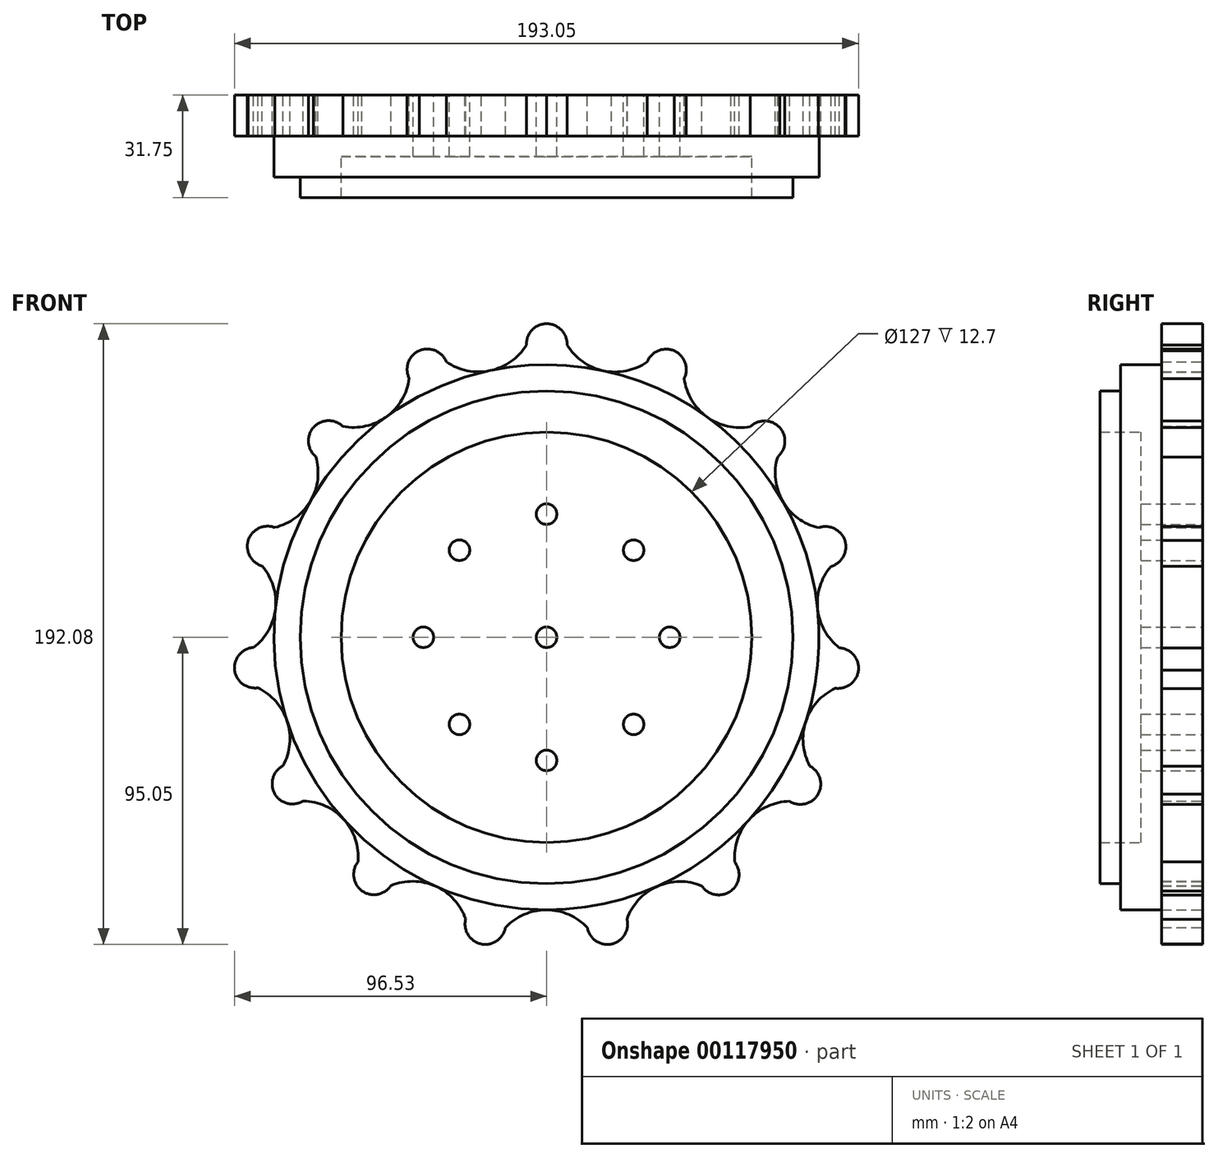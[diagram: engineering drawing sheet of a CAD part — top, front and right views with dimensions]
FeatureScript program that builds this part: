
annotation { "Feature Type Name" : "Feature", "Feature Type Description" : "" }
export const myFeature = defineFeature(function(context is Context, id is Id, definition is map)
    precondition{}
    {
        {
            var Q0;
            Q0=qCreatedBy(makeId("Front.planeOp"),FACE);
            var sketch = newSketch(context, id + "F0", { "sketchPlane" : qUnion([Q0])});
            skCircle(sketch, "E0", {"center": v(0, 0) * mm, "radius": 84.33 * mm});
            skCircle(sketch, "E1", {"center": v(0, 0) * mm, "radius": 97.03 * mm, "construction": true});
            skLineSegment(sketch, "E2", {"start": v(0, 84.33) * mm, "end": v(0, 97.03) * mm, "construction": true});
            skPoint(sketch, "E3", {"position": v(0, 90.68) * mm});
            skCircle(sketch, "E4", {"center": v(0, 0) * mm, "radius": 90.68 * mm, "construction": true});
            skArc(sketch, "E5", {"start": v(0, 90.68) * mm, "mid": v(0, 90.46) * mm, "end": v(0, 90.23) * mm});
            skPoint(sketch, "E6", {"position": v(0, 84.33) * mm});
            skPoint(sketch, "E7", {"position": v(-6.35, 90.46) * mm});
            skPoint(sketch, "E8", {"position": v(17.59, 82.47) * mm});
            skArc(sketch, "E9", {"start": v(6.35, 90.46) * mm, "mid": v(17.59, 82.47) * mm, "end": v(31.11, 85.17) * mm});
            skArc(sketch, "E10", {"start": v(6.35, 90.46) * mm, "mid": v(4.57, 95.09) * mm, "end": v(0, 97.03) * mm});
            skPoint(sketch, "E11", {"position": v(39.59, 88.59) * mm});
            skArc(sketch, "E12", {"start": v(39.59, 88.59) * mm, "mid": v(34.62, 88.68) * mm, "end": v(31.11, 85.17) * mm});
            skArc(sketch, "E13.1.0", {"start": v(-31, 85.22) * mm, "mid": v(-34.5, 88.73) * mm, "end": v(-39.46, 88.64) * mm});
            skArc(sketch, "E13.1.1", {"start": v(-31, 85.22) * mm, "mid": v(-17.48, 82.5) * mm, "end": v(-6.22, 90.46) * mm});
            skArc(sketch, "E13.1.2", {"start": v(0.13, 97.03) * mm, "mid": v(-4.44, 95.1) * mm, "end": v(-6.22, 90.46) * mm});
            skArc(sketch, "E13.2.0", {"start": v(-62.98, 65.24) * mm, "mid": v(-67.6, 67.02) * mm, "end": v(-72.1, 64.92) * mm});
            skArc(sketch, "E13.2.1", {"start": v(-62.98, 65.24) * mm, "mid": v(-49.52, 68.26) * mm, "end": v(-42.48, 80.11) * mm});
            skArc(sketch, "E13.2.2", {"start": v(-39.34, 88.7) * mm, "mid": v(-42.73, 85.07) * mm, "end": v(-42.48, 80.11) * mm});
            skArc(sketch, "E13.3.0", {"start": v(-84.07, 33.99) * mm, "mid": v(-89.02, 33.73) * mm, "end": v(-92.28, 29.98) * mm});
            skArc(sketch, "E13.3.1", {"start": v(-84.07, 33.99) * mm, "mid": v(-73, 42.21) * mm, "end": v(-71.4, 55.9) * mm});
            skArc(sketch, "E13.3.2", {"start": v(-72.02, 65.02) * mm, "mid": v(-73.64, 60.33) * mm, "end": v(-71.4, 55.9) * mm});
            skArc(sketch, "E13.4.0", {"start": v(-90.62, -3.14) * mm, "mid": v(-95.05, -5.4) * mm, "end": v(-96.5, -10.14) * mm});
            skArc(sketch, "E13.4.1", {"start": v(-90.62, -3.14) * mm, "mid": v(-83.86, 8.87) * mm, "end": v(-87.96, 22.04) * mm});
            skArc(sketch, "E13.4.2", {"start": v(-92.24, 30.11) * mm, "mid": v(-91.81, 25.17) * mm, "end": v(-87.96, 22.04) * mm});
            skArc(sketch, "E13.5.0", {"start": v(-81.5, -39.73) * mm, "mid": v(-84.63, -43.59) * mm, "end": v(-84.03, -48.51) * mm});
            skArc(sketch, "E13.5.1", {"start": v(-81.5, -39.73) * mm, "mid": v(-80.22, -26) * mm, "end": v(-89.32, -15.64) * mm});
            skArc(sketch, "E13.5.2", {"start": v(-96.51, -10) * mm, "mid": v(-94.11, -14.35) * mm, "end": v(-89.32, -15.64) * mm});
            skArc(sketch, "E13.6.0", {"start": v(-58.3, -69.45) * mm, "mid": v(-59.59, -74.24) * mm, "end": v(-57.03, -78.5) * mm});
            skArc(sketch, "E13.6.1", {"start": v(-58.3, -69.45) * mm, "mid": v(-62.7, -56.38) * mm, "end": v(-75.23, -50.62) * mm});
            skArc(sketch, "E13.6.2", {"start": v(-84.1, -48.4) * mm, "mid": v(-80.14, -51.4) * mm, "end": v(-75.23, -50.62) * mm});
            skArc(sketch, "E13.7.0", {"start": v(-25.01, -87.16) * mm, "mid": v(-24.24, -92.06) * mm, "end": v(-20.17, -94.9) * mm});
            skArc(sketch, "E13.7.1", {"start": v(-25.01, -87.16) * mm, "mid": v(-34.35, -77.01) * mm, "end": v(-48.14, -76.84) * mm});
            skArc(sketch, "E13.7.2", {"start": v(-57.14, -78.42) * mm, "mid": v(-52.3, -79.54) * mm, "end": v(-48.14, -76.84) * mm});
            skArc(sketch, "E13.8.0", {"start": v(12.6, -89.8) * mm, "mid": v(15.3, -93.96) * mm, "end": v(20.17, -94.9) * mm});
            skArc(sketch, "E13.8.1", {"start": v(12.6, -89.8) * mm, "mid": v(-0.06, -84.33) * mm, "end": v(-12.72, -89.78) * mm});
            skArc(sketch, "E13.8.2", {"start": v(-20.3, -94.88) * mm, "mid": v(-15.43, -93.94) * mm, "end": v(-12.72, -89.78) * mm});
            skArc(sketch, "E13.9.0", {"start": v(48.03, -76.91) * mm, "mid": v(52.2, -79.61) * mm, "end": v(57.03, -78.5) * mm});
            skArc(sketch, "E13.9.1", {"start": v(48.03, -76.91) * mm, "mid": v(34.25, -77.06) * mm, "end": v(24.9, -87.2) * mm});
            skArc(sketch, "E13.9.2", {"start": v(20.04, -94.94) * mm, "mid": v(24.11, -92.1) * mm, "end": v(24.9, -87.2) * mm});
            skArc(sketch, "E13.10.0", {"start": v(75.16, -50.72) * mm, "mid": v(80.07, -51.5) * mm, "end": v(84.03, -48.51) * mm});
            skArc(sketch, "E13.10.1", {"start": v(75.16, -50.72) * mm, "mid": v(62.63, -56.47) * mm, "end": v(58.2, -69.53) * mm});
            skArc(sketch, "E13.10.2", {"start": v(56.92, -78.58) * mm, "mid": v(59.49, -74.33) * mm, "end": v(58.2, -69.53) * mm});
            skArc(sketch, "E13.11.0", {"start": v(89.3, -15.77) * mm, "mid": v(94.1, -14.48) * mm, "end": v(96.5, -10.14) * mm});
            skArc(sketch, "E13.11.1", {"start": v(89.3, -15.77) * mm, "mid": v(80.18, -26.11) * mm, "end": v(81.46, -39.84) * mm});
            skArc(sketch, "E13.11.2", {"start": v(83.96, -48.63) * mm, "mid": v(84.57, -43.7) * mm, "end": v(81.46, -39.84) * mm});
            skArc(sketch, "E13.12.0", {"start": v(87.99, 21.92) * mm, "mid": v(91.85, 25.04) * mm, "end": v(92.28, 29.98) * mm});
            skArc(sketch, "E13.12.1", {"start": v(87.99, 21.92) * mm, "mid": v(83.87, 8.76) * mm, "end": v(90.62, -3.27) * mm});
            skArc(sketch, "E13.12.2", {"start": v(96.48, -10.27) * mm, "mid": v(95.04, -5.53) * mm, "end": v(90.62, -3.27) * mm});
            skArc(sketch, "E13.13.0", {"start": v(71.47, 55.81) * mm, "mid": v(73.72, 60.23) * mm, "end": v(72.1, 64.92) * mm});
            skArc(sketch, "E13.13.1", {"start": v(71.47, 55.81) * mm, "mid": v(73.06, 42.11) * mm, "end": v(84.11, 33.87) * mm});
            skArc(sketch, "E13.13.2", {"start": v(92.32, 29.86) * mm, "mid": v(89.07, 33.6) * mm, "end": v(84.11, 33.87) * mm});
            skArc(sketch, "E13.14.0", {"start": v(42.59, 80.05) * mm, "mid": v(42.85, 85) * mm, "end": v(39.46, 88.64) * mm});
            skArc(sketch, "E13.14.1", {"start": v(42.59, 80.05) * mm, "mid": v(49.61, 68.19) * mm, "end": v(63.06, 65.16) * mm});
            skArc(sketch, "E13.14.2", {"start": v(72.2, 64.83) * mm, "mid": v(67.7, 66.93) * mm, "end": v(63.06, 65.16) * mm});
            skCircle(sketch, "E14", {"center": v(0, 0) * mm, "radius": 76.2 * mm});
            skCircle(sketch, "E15", {"center": v(0, 0) * mm, "radius": 63.5 * mm});
            skCircle(sketch, "E16", {"center": v(0, 0) * mm, "radius": 38.1 * mm, "construction": true});
            skPoint(sketch, "E17", {"position": v(0, 38.1) * mm});
            skCircle(sketch, "E18", {"center": v(0, 38.1) * mm, "radius": 3.18 * mm});
            skCircle(sketch, "E19.1.0", {"center": v(-26.94, 26.94) * mm, "radius": 3.18 * mm});
            skCircle(sketch, "E19.2.0", {"center": v(-38.1, 0) * mm, "radius": 3.18 * mm});
            skCircle(sketch, "E19.3.0", {"center": v(-26.94, -26.94) * mm, "radius": 3.18 * mm});
            skCircle(sketch, "E19.4.0", {"center": v(0, -38.1) * mm, "radius": 3.18 * mm});
            skCircle(sketch, "E19.5.0", {"center": v(26.94, -26.94) * mm, "radius": 3.18 * mm});
            skCircle(sketch, "E19.6.0", {"center": v(38.1, 0) * mm, "radius": 3.18 * mm});
            skCircle(sketch, "E19.7.0", {"center": v(26.94, 26.94) * mm, "radius": 3.18 * mm});
            skCircle(sketch, "E20", {"center": v(0, 0) * mm, "radius": 3.18 * mm});
            skSolve(sketch);
        }
        {
            var Q0;
            Q0=makeQuery(id+"F0.imprint","IMPRINT",FACE,{"disambiguationData":[TD([[makeQuery(id+"F0.imprint","IMPRINT",EDGE,{"derivedFrom":sQuery(id+"F0.wireOp",EDGE,"E14")}),-1.0]])]});
            extrude(context, id + "F1", {"entities" : qUnion([Q0]), "depth" : 25.4 * mm});
        }
        {
            var Q0;
            Q0=makeQuery(id+"F0.imprint","IMPRINT",FACE,{"disambiguationData":[TD([[makeQuery(id+"F0.imprint","IMPRINT",EDGE,{"derivedFrom":sQuery(id+"F0.wireOp",EDGE,"E14")}),1.0]])]});
            extrude(context, id + "F2", {"entities" : qUnion([Q0]), "operationType" : NewBodyOperationType.ADD, "depth" : 31.75 * mm});
        }
        {
            var Q0;
            Q0=makeQuery(id+"F0.imprint","IMPRINT",FACE,{"disambiguationData":[TD([[makeQuery(id+"F0.imprint","IMPRINT",EDGE,{"derivedFrom":sQuery(id+"F0.wireOp",EDGE,"E15")}),1.0]])]});
            extrude(context, id + "F3", {"entities" : qUnion([Q0]), "operationType" : NewBodyOperationType.ADD, "depth" : 19.05 * mm});
        }
        {
            var Q0;
            {var subQ3=sQuery(id+"F0.wireOp",EDGE,"E0");var subQ5=sQuery(id+"F0.wireOp",EDGE,"E13.3.1");var subQ8=makeQuery(id+"F0.imprint","INTERSECT",VERTEX,{"derivedFrom":[subQ3,subQ5]});Q0=makeQuery(id+"F0.imprint","IMPRINT",FACE,{"disambiguationData":[TD([[makeQuery(id+"F0.imprint","IMPRINT",EDGE,{"disambiguationData":[TD([[subQ8,-1.0]])],"derivedFrom":subQ3}),-1.0]])]});}
            var Q1;
            {var subQ0=sQuery(id+"F0.wireOp",EDGE,"E13.4.1");var subQ3=sQuery(id+"F0.wireOp",EDGE,"E0");var subQ4=makeQuery(id+"F0.imprint","INTERSECT",VERTEX,{"derivedFrom":[subQ3,subQ0]});Q1=makeQuery(id+"F0.imprint","IMPRINT",FACE,{"disambiguationData":[TD([[makeQuery(id+"F0.imprint","IMPRINT",EDGE,{"disambiguationData":[TD([[subQ4,-1.0]])],"derivedFrom":subQ3}),-1.0]])]});}
            var Q2;
            {var subQ3=sQuery(id+"F0.wireOp",EDGE,"E0");var subQ5=sQuery(id+"F0.wireOp",EDGE,"E13.6.1");var subQ9=makeQuery(id+"F0.imprint","INTERSECT",VERTEX,{"derivedFrom":[subQ3,subQ5]});Q2=makeQuery(id+"F0.imprint","IMPRINT",FACE,{"disambiguationData":[TD([[makeQuery(id+"F0.imprint","IMPRINT",EDGE,{"disambiguationData":[TD([[subQ9,-1.0]])],"derivedFrom":subQ3}),-1.0]])]});}
            var Q3;
            {var subQ0=sQuery(id+"F0.wireOp",EDGE,"E13.5.1");var subQ3=sQuery(id+"F0.wireOp",EDGE,"E0");var subQ4=makeQuery(id+"F0.imprint","INTERSECT",VERTEX,{"derivedFrom":[subQ3,subQ0]});Q3=makeQuery(id+"F0.imprint","IMPRINT",FACE,{"disambiguationData":[TD([[makeQuery(id+"F0.imprint","IMPRINT",EDGE,{"disambiguationData":[TD([[subQ4,-1.0]])],"derivedFrom":subQ3}),-1.0]])]});}
            var Q4;
            {var subQ3=sQuery(id+"F0.wireOp",EDGE,"E0");var subQ5=sQuery(id+"F0.wireOp",EDGE,"E13.7.1");var subQ8=makeQuery(id+"F0.imprint","INTERSECT",VERTEX,{"derivedFrom":[subQ3,subQ5]});Q4=makeQuery(id+"F0.imprint","IMPRINT",FACE,{"disambiguationData":[TD([[makeQuery(id+"F0.imprint","IMPRINT",EDGE,{"disambiguationData":[TD([[subQ8,-1.0]])],"derivedFrom":subQ3}),-1.0]])]});}
            var Q5;
            {var subQ3=sQuery(id+"F0.wireOp",EDGE,"E0");var subQ5=sQuery(id+"F0.wireOp",EDGE,"E13.8.1");var subQ8=makeQuery(id+"F0.imprint","INTERSECT",VERTEX,{"derivedFrom":[subQ3,subQ5]});Q5=makeQuery(id+"F0.imprint","IMPRINT",FACE,{"disambiguationData":[TD([[makeQuery(id+"F0.imprint","IMPRINT",EDGE,{"disambiguationData":[TD([[subQ8,-1.0]])],"derivedFrom":subQ3}),-1.0]])]});}
            var Q6;
            {var subQ0=sQuery(id+"F0.wireOp",EDGE,"E13.9.1");var subQ3=sQuery(id+"F0.wireOp",EDGE,"E0");var subQ4=makeQuery(id+"F0.imprint","INTERSECT",VERTEX,{"derivedFrom":[subQ3,subQ0]});Q6=makeQuery(id+"F0.imprint","IMPRINT",FACE,{"disambiguationData":[TD([[makeQuery(id+"F0.imprint","IMPRINT",EDGE,{"disambiguationData":[TD([[subQ4,-1.0]])],"derivedFrom":subQ3}),-1.0]])]});}
            var Q7;
            {var subQ3=sQuery(id+"F0.wireOp",EDGE,"E0");var subQ5=sQuery(id+"F0.wireOp",EDGE,"E13.10.1");var subQ8=makeQuery(id+"F0.imprint","INTERSECT",VERTEX,{"derivedFrom":[subQ3,subQ5]});Q7=makeQuery(id+"F0.imprint","IMPRINT",FACE,{"disambiguationData":[TD([[makeQuery(id+"F0.imprint","IMPRINT",EDGE,{"disambiguationData":[TD([[subQ8,-1.0]])],"derivedFrom":subQ3}),-1.0]])]});}
            var Q8;
            {var subQ1=sQuery(id+"F0.wireOp",EDGE,"E13.12.1");var subQ3=sQuery(id+"F0.wireOp",EDGE,"E0");var subQ4=makeQuery(id+"F0.imprint","INTERSECT",VERTEX,{"derivedFrom":[subQ3,subQ1]});Q8=makeQuery(id+"F0.imprint","IMPRINT",FACE,{"disambiguationData":[TD([[makeQuery(id+"F0.imprint","IMPRINT",EDGE,{"disambiguationData":[TD([[subQ4,1.0]])],"derivedFrom":subQ3}),-1.0]])]});}
            var Q9;
            {var subQ3=sQuery(id+"F0.wireOp",EDGE,"E0");var subQ7=sQuery(id+"F0.wireOp",EDGE,"E13.13.1");var subQ9=makeQuery(id+"F0.imprint","INTERSECT",VERTEX,{"derivedFrom":[subQ3,subQ7]});Q9=makeQuery(id+"F0.imprint","IMPRINT",FACE,{"disambiguationData":[TD([[makeQuery(id+"F0.imprint","IMPRINT",EDGE,{"disambiguationData":[TD([[subQ9,1.0]])],"derivedFrom":subQ3}),-1.0]])]});}
            var Q10;
            {var subQ3=sQuery(id+"F0.wireOp",EDGE,"E0");var subQ5=sQuery(id+"F0.wireOp",EDGE,"E13.13.1");var subQ9=makeQuery(id+"F0.imprint","INTERSECT",VERTEX,{"derivedFrom":[subQ3,subQ5]});Q10=makeQuery(id+"F0.imprint","IMPRINT",FACE,{"disambiguationData":[TD([[makeQuery(id+"F0.imprint","IMPRINT",EDGE,{"disambiguationData":[TD([[subQ9,-1.0]])],"derivedFrom":subQ3}),-1.0]])]});}
            var Q11;
            {var subQ0=sQuery(id+"F0.wireOp",EDGE,"E13.14.1");var subQ7=sQuery(id+"F0.wireOp",EDGE,"E0");var subQ9=makeQuery(id+"F0.imprint","INTERSECT",VERTEX,{"derivedFrom":[subQ7,subQ0]});Q11=makeQuery(id+"F0.imprint","IMPRINT",FACE,{"disambiguationData":[TD([[makeQuery(id+"F0.imprint","IMPRINT",EDGE,{"disambiguationData":[TD([[subQ9,-1.0]])],"derivedFrom":subQ7}),-1.0]])]});}
            var Q12;
            {var subQ3=sQuery(id+"F0.wireOp",EDGE,"E0");var subQ6=sQuery(id+"F0.wireOp",EDGE,"E9");var subQ8=makeQuery(id+"F0.imprint","INTERSECT",VERTEX,{"derivedFrom":[subQ3,subQ6]});Q12=makeQuery(id+"F0.imprint","IMPRINT",FACE,{"disambiguationData":[TD([[makeQuery(id+"F0.imprint","IMPRINT",EDGE,{"disambiguationData":[TD([[subQ8,-1.0]])],"derivedFrom":subQ3}),-1.0]])]});}
            var Q13;
            {var subQ3=sQuery(id+"F0.wireOp",EDGE,"E0");var subQ5=sQuery(id+"F0.wireOp",EDGE,"E13.1.1");var subQ8=makeQuery(id+"F0.imprint","INTERSECT",VERTEX,{"derivedFrom":[subQ3,subQ5]});Q13=makeQuery(id+"F0.imprint","IMPRINT",FACE,{"disambiguationData":[TD([[makeQuery(id+"F0.imprint","IMPRINT",EDGE,{"disambiguationData":[TD([[subQ8,-1.0]])],"derivedFrom":subQ3}),-1.0]])]});}
            var Q14;
            {var subQ3=sQuery(id+"F0.wireOp",EDGE,"E0");var subQ5=sQuery(id+"F0.wireOp",EDGE,"E13.2.1");var subQ9=makeQuery(id+"F0.imprint","INTERSECT",VERTEX,{"derivedFrom":[subQ3,subQ5]});Q14=makeQuery(id+"F0.imprint","IMPRINT",FACE,{"disambiguationData":[TD([[makeQuery(id+"F0.imprint","IMPRINT",EDGE,{"disambiguationData":[TD([[subQ9,-1.0]])],"derivedFrom":subQ3}),-1.0]])]});}
            extrude(context, id + "F4", {"entities" : qUnion([Q0, Q1, Q2, Q3, Q4, Q5, Q6, Q7, Q8, Q9, Q10, Q11, Q12, Q13, Q14]), "operationType" : NewBodyOperationType.ADD, "depth" : 12.7 * mm});
        }
    });
